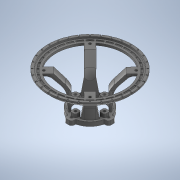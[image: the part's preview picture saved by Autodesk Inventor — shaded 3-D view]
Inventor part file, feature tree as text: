
AUTODESK INVENTOR PART (.ipt)
format: ipt  version: 2020 (Build 240168000, 168)  size: 1,970,688 bytes
history: native  units: mm
features: sketch x22, projected_geometry x22, other x20, extrude x10, revolve x9, pattern_circular x6, loft x5, fillet x4, chamfer x1, mirror x1
ambient origin geometry x8: Origin, YZ Plane, XZ Plane, XY Plane, X Axis, Y Axis, Z Axis, Center Point
bodies: Body1 (feature_tree)
feature tree (100):
  other  "Твердое тело1"
  extrude  "Выдавливание1"  Depth=34.0mm
  other  "РабПлоскость1"
  other  "РабОсь1"
  revolve  "Вращение1"
  sketch  "Эскиз3"
  other  "РабТочка1"
  extrude  "Выдавливание2"  Depth=45.0mm
  other  "РабТочка2"
  other  "РабТочка3"
  other  "РабТочка4"
  other  "РабПлоскость2"
  sketch  "Эскиз5"
  revolve  "Вращение2"
  revolve  "Вращение3"
  pattern_circular  "Круговой массив1"  Angle=45.0deg  [1 undecoded]
  extrude  "Выдавливание3"  Depth=2.9mm
  revolve  "Вращение4"
  sketch  "Эскиз8"
  fillet  "Сопряжение1"  Radius=9.0mm
  revolve  "Вращение5"
  other  "РабПлоскость6"
  other  "РабПлоскость7"
  sketch  "Эскиз10"
  revolve  "Вращение6"
  revolve  "Вращение7"
  sketch  "Эскиз11"
  sketch  "Эскиз12"
  loft  "Лофт2"
  loft  "Лофт3"
  fillet  "Сопряжение2"  Radius=1.0mm
  extrude  "Выдавливание4"  Depth=22.0mm
  loft  "Лофт4"
  fillet  "Сопряжение3"  Radius=5.0mm
  pattern_circular  "Круговой массив2"  [2 undecoded]
  revolve  "Вращение8"
  revolve  "Вращение9"
  extrude  "Выдавливание5"  Depth=2.5mm
  extrude  "Выдавливание6"  Depth=45.0mm
  pattern_circular  "Круговой массив3"  [2 undecoded]
  other  "РабПлоскость8"
  extrude  "Выдавливание8"  Depth=2.0mm
  extrude  "Выдавливание7"  Depth=2.0mm
  loft  "Лофт5"
  pattern_circular  "Круговой массив4"  Angle=45.0deg  [1 undecoded]
  fillet  "Сопряжение4"  [1 undecoded]
  chamfer  "Фаска1"  Distance=3.0mm
  sketch  "Эскиз23"
  extrude  "Выдавливание9"  TaperAngle=135.0deg  [1 undecoded]
  loft  "Лофт6"
  other  "РабПлоскость9"
  mirror  "Зеркальное отражение1"
  pattern_circular  "Круговой массив5"  [2 undecoded]
  extrude  "Выдавливание10"  TaperAngle=0.0deg  [1 undecoded]
  pattern_circular  "Круговой массив6"  [2 undecoded]
  sketch  "Эскиз1"
  sketch  "Эскиз2"
  sketch  "Эскиз4"
  projected_geometry  "Спроецированная петля1"
  projected_geometry  "Спроецированная петля2"
  projected_geometry  "Спроецированная петля3"
  other  "РабПлоскость3"
  other  "РабПлоскость4"
  other  "РабПлоскость5"
  sketch  "Эскиз6"
  sketch  "Эскиз7"
  sketch  "Эскиз9"
  projected_geometry  "Спроецированная петля4"
  projected_geometry  "Спроецированная петля5"
  other  "Ребра2"
  other  "Ребра3"
  other  "Ребра4"
  sketch  "Эскиз13"
  projected_geometry  "Спроецированная петля6"
  projected_geometry  "Спроецированная петля7"
  sketch  "Эскиз14"
  projected_geometry  "Спроецированная петля8"
  projected_geometry  "Спроецированная петля9"
  projected_geometry  "Спроецированная петля10"
  sketch  "Эскиз16"
  sketch  "Эскиз17"
  projected_geometry  "Спроецированная петля12"
  projected_geometry  "Спроецированная петля13"
  sketch  "Эскиз18"
  sketch  "Эскиз19"
  projected_geometry  "Спроецированная петля14"
  projected_geometry  "Спроецированная петля15"
  other  "Ребра5"
  sketch  "Эскиз22"
  projected_geometry  "Спроецированная петля16"
  projected_geometry  "Спроецированная петля17"
  projected_geometry  "Спроецированная петля18"
  projected_geometry  "Спроецированная петля19"
  projected_geometry  "Спроецированная петля20"
  sketch  "Эскиз24"
  other  "Ребра6"
  sketch  "Эскиз25"
  projected_geometry  "Спроецированная петля21"
  projected_geometry  "Спроецированная петля22"
  projected_geometry  "Спроецированная петля23"
note: 13 required parameter values undecoded (feature->parameter linkage not recoverable at this tier; creation-order binding heuristic only, values carry confidence <= 0.55)
